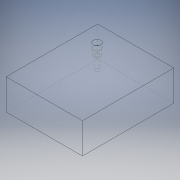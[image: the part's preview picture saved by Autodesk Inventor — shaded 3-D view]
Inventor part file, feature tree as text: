
AUTODESK INVENTOR PART (.ipt)
format: ipt  version: 2018 (Build 220112000, 112)  size: 325,632 bytes
history: native  units: mm (DEFAULTED — no unit token found)
features: extrude x4, other x4, sketch x2, fillet x1, loft x1
ambient origin geometry x8: Origin, YZ Plane, XZ Plane, XY Plane, X Axis, Y Axis, Z Axis, Center Point
bodies: Solid1 (feature_tree)
feature tree (12):
  extrude  "Extrusion1"  Depth=25.4mm
  sketch  "Sketch2"  dims[d2=76.2mm d3=0.0mm d4=3.3147mm d5=6.2865mm d6=5.588mm d7=19.812mm d8=0.0mm d9=9.398mm d10=0.0mm d11=4.1148mm d12=0.0mm d13=1.8288mm d14=0.0mm d15=90.0deg d16=0.0mm d17=90.0deg d18=0.0mm d19=90.0deg d20=0.0mm d21=90.0deg d22=8.89mm d23=8.89mm d24=8.89mm]
  extrude  "Extrusion2"  Depth=4.1148mm
  extrude  "Extrusion3"  Depth=4.1148mm
  extrude  "Extrusion4"  Depth=5.588mm
  fillet  "Fillet1"  Radius=19.812mm
  loft  "Loft1"
  sketch  "Sketch1"  dims[d0=63.5mm d1=25.4mm]
  other  "Edges1"
  other  "Edges2"
  other  "Edges3"
  other  "Edges4"
